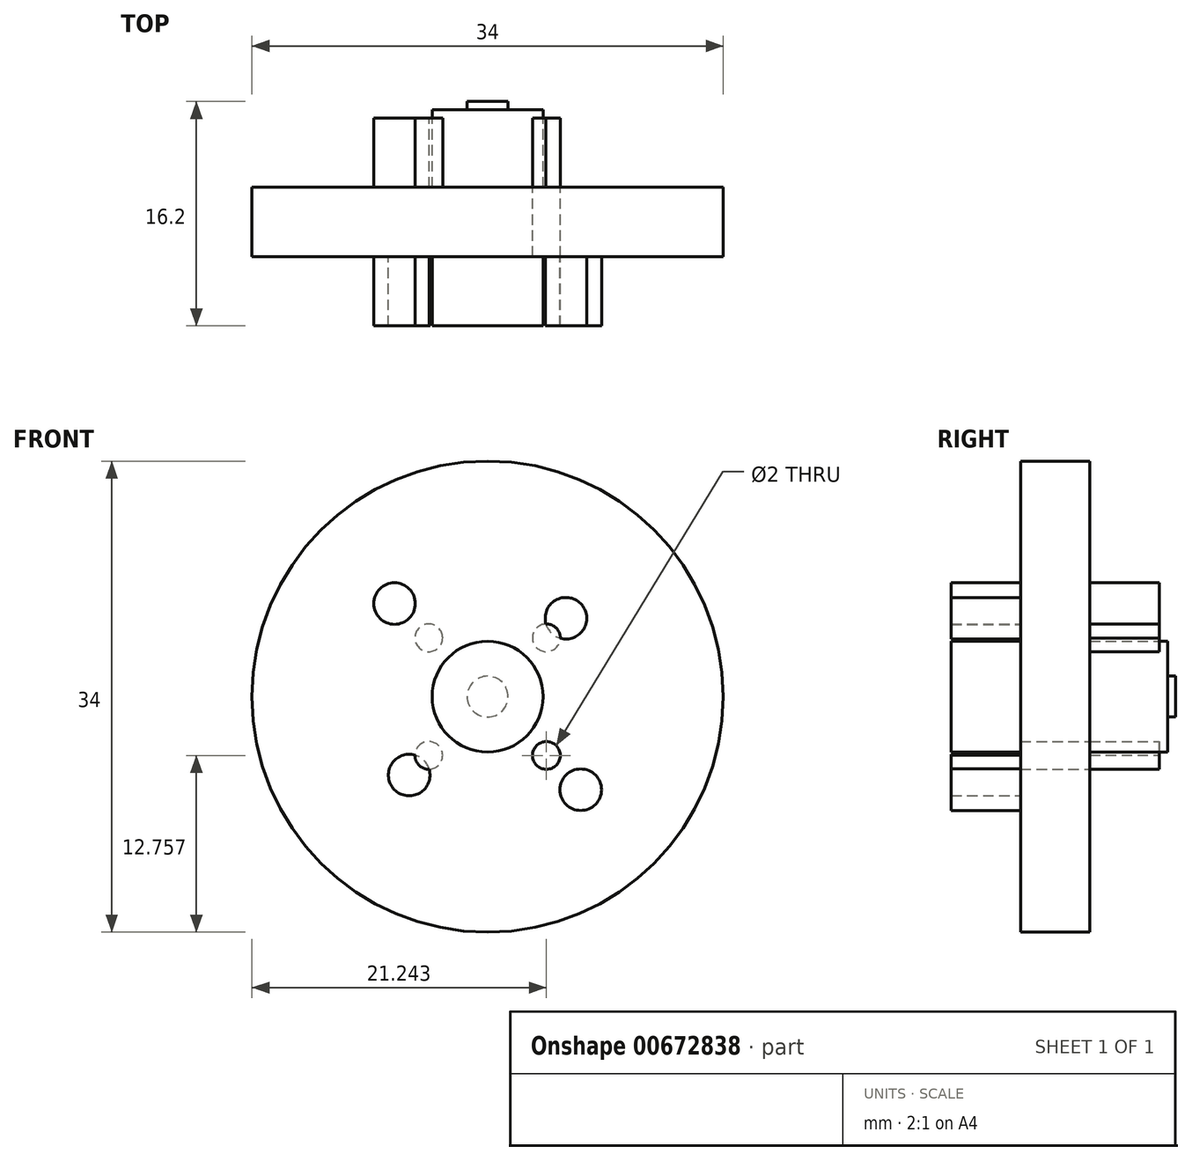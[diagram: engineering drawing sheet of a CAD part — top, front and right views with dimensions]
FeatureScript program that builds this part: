
annotation { "Feature Type Name" : "Feature", "Feature Type Description" : "" }
export const myFeature = defineFeature(function(context is Context, id is Id, definition is map)
    precondition{}
    {
        {
            var Q0;
            Q0=qCreatedBy(makeId("Front.planeOp"),FACE);
            var sketch = newSketch(context, id + "F0", { "sketchPlane" : qUnion([Q0])});
            skCircle(sketch, "E0", {"center": v(0, 0) * mm, "radius": 17 * mm});
            skCircle(sketch, "E1", {"center": v(5.66, 5.66) * mm, "radius": 1.5 * mm});
            skCircle(sketch, "E2.MirrorC", {"center": v(-6.72, 6.72) * mm, "radius": 1.5 * mm});
            skCircle(sketch, "E3.MirrorC", {"center": v(-5.66, -5.66) * mm, "radius": 1.5 * mm});
            skLineSegment(sketch, "E4", {"start": v(0, 29.65) * mm, "end": v(0, -28.8) * mm, "construction": true});
            skLineSegment(sketch, "E5", {"start": v(-6.72, 6.72) * mm, "end": v(4.6, -4.6) * mm, "construction": true});
            skLineSegment(sketch, "E6", {"start": v(5.66, 5.66) * mm, "end": v(-5.66, -5.66) * mm, "construction": true});
            skCircle(sketch, "E7", {"center": v(-4.24, 4.24) * mm, "radius": 1 * mm});
            skCircle(sketch, "E8.MirrorC", {"center": v(4.24, 4.24) * mm, "radius": 1 * mm});
            skCircle(sketch, "E9.MirrorC", {"center": v(4.24, -4.24) * mm, "radius": 1 * mm});
            skCircle(sketch, "E10.MirrorC", {"center": v(-4.24, -4.24) * mm, "radius": 1 * mm});
            skCircle(sketch, "E11.MirrorC", {"center": v(6.72, -6.72) * mm, "radius": 1.5 * mm});
            skCircle(sketch, "E12", {"center": v(0, 0) * mm, "radius": 1.48 * mm});
            skCircle(sketch, "E13", {"center": v(0, 0) * mm, "radius": 4 * mm});
            skSolve(sketch);
        }
        {
            var Q0;
            Q0=makeQuery(id+"F0.imprint","IMPRINT",FACE,{"disambiguationData":[TD([[makeQuery(id+"F0.imprint","IMPRINT",EDGE,{"derivedFrom":sQuery(id+"F0.wireOp",EDGE,"E0")}),1.0]])]});
            var Q1;
            {var subQ0=sQuery(id+"F0.wireOp",EDGE,"E7");var subQ1=sQuery(id+"F0.wireOp",EDGE,"E2.MirrorC");var subQ2=makeQuery(id+"F0.imprint","INTERSECT",VERTEX,{"disambiguationData":[OD(0.0)],"derivedFrom":[subQ1,subQ0]});Q1=makeQuery(id+"F0.imprint","IMPRINT",FACE,{"disambiguationData":[TD([[makeQuery(id+"F0.imprint","IMPRINT",EDGE,{"disambiguationData":[TD([[subQ2,-1.0]])],"derivedFrom":subQ1}),-1.0]])]});}
            var Q2;
            {var subQ0=sQuery(id+"F0.wireOp",EDGE,"E8.MirrorC");var subQ1=sQuery(id+"F0.wireOp",EDGE,"E1");var subQ2=makeQuery(id+"F0.imprint","INTERSECT",VERTEX,{"disambiguationData":[OD(0.0)],"derivedFrom":[subQ1,subQ0]});Q2=makeQuery(id+"F0.imprint","IMPRINT",FACE,{"disambiguationData":[TD([[makeQuery(id+"F0.imprint","IMPRINT",EDGE,{"disambiguationData":[TD([[subQ2,1.0]])],"derivedFrom":subQ1}),1.0]])]});}
            var Q3;
            {var subQ0=sQuery(id+"F0.wireOp",EDGE,"E8.MirrorC");var subQ1=sQuery(id+"F0.wireOp",EDGE,"E1");var subQ2=makeQuery(id+"F0.imprint","INTERSECT",VERTEX,{"disambiguationData":[OD(0.0)],"derivedFrom":[subQ1,subQ0]});Q3=makeQuery(id+"F0.imprint","IMPRINT",FACE,{"disambiguationData":[TD([[makeQuery(id+"F0.imprint","IMPRINT",EDGE,{"disambiguationData":[TD([[subQ2,-1.0]])],"derivedFrom":subQ1}),-1.0]])]});}
            var Q4;
            {var subQ0=sQuery(id+"F0.wireOp",EDGE,"E7");var subQ1=sQuery(id+"F0.wireOp",EDGE,"E2.MirrorC");var subQ2=makeQuery(id+"F0.imprint","INTERSECT",VERTEX,{"disambiguationData":[OD(0.0)],"derivedFrom":[subQ1,subQ0]});Q4=makeQuery(id+"F0.imprint","IMPRINT",FACE,{"disambiguationData":[TD([[makeQuery(id+"F0.imprint","IMPRINT",EDGE,{"disambiguationData":[TD([[subQ2,1.0]])],"derivedFrom":subQ1}),-1.0]])]});}
            var Q5;
            {var subQ0=sQuery(id+"F0.wireOp",EDGE,"E7");var subQ1=sQuery(id+"F0.wireOp",EDGE,"E2.MirrorC");var subQ2=makeQuery(id+"F0.imprint","INTERSECT",VERTEX,{"disambiguationData":[OD(0.0)],"derivedFrom":[subQ1,subQ0]});Q5=makeQuery(id+"F0.imprint","IMPRINT",FACE,{"disambiguationData":[TD([[makeQuery(id+"F0.imprint","IMPRINT",EDGE,{"disambiguationData":[TD([[subQ2,1.0]])],"derivedFrom":subQ1}),1.0]])]});}
            var Q6;
            {var subQ0=sQuery(id+"F0.wireOp",EDGE,"E10.MirrorC");var subQ1=sQuery(id+"F0.wireOp",EDGE,"E3.MirrorC");var subQ2=makeQuery(id+"F0.imprint","INTERSECT",VERTEX,{"disambiguationData":[OD(0.0)],"derivedFrom":[subQ1,subQ0]});Q6=makeQuery(id+"F0.imprint","IMPRINT",FACE,{"disambiguationData":[TD([[makeQuery(id+"F0.imprint","IMPRINT",EDGE,{"disambiguationData":[TD([[subQ2,-1.0]])],"derivedFrom":subQ1}),1.0]])]});}
            var Q7;
            {var subQ0=sQuery(id+"F0.wireOp",EDGE,"E10.MirrorC");var subQ1=sQuery(id+"F0.wireOp",EDGE,"E3.MirrorC");var subQ2=makeQuery(id+"F0.imprint","INTERSECT",VERTEX,{"disambiguationData":[OD(0.0)],"derivedFrom":[subQ1,subQ0]});Q7=makeQuery(id+"F0.imprint","IMPRINT",FACE,{"disambiguationData":[TD([[makeQuery(id+"F0.imprint","IMPRINT",EDGE,{"disambiguationData":[TD([[subQ2,1.0]])],"derivedFrom":subQ1}),1.0]])]});}
            var Q8;
            {var subQ0=sQuery(id+"F0.wireOp",EDGE,"E10.MirrorC");var subQ1=sQuery(id+"F0.wireOp",EDGE,"E3.MirrorC");var subQ2=makeQuery(id+"F0.imprint","INTERSECT",VERTEX,{"disambiguationData":[OD(0.0)],"derivedFrom":[subQ1,subQ0]});Q8=makeQuery(id+"F0.imprint","IMPRINT",FACE,{"disambiguationData":[TD([[makeQuery(id+"F0.imprint","IMPRINT",EDGE,{"disambiguationData":[TD([[subQ2,1.0]])],"derivedFrom":subQ1}),-1.0]])]});}
            var Q9;
            {var subQ0=sQuery(id+"F0.wireOp",EDGE,"E8.MirrorC");var subQ1=sQuery(id+"F0.wireOp",EDGE,"E1");var subQ2=makeQuery(id+"F0.imprint","INTERSECT",VERTEX,{"disambiguationData":[OD(0.0)],"derivedFrom":[subQ1,subQ0]});Q9=makeQuery(id+"F0.imprint","IMPRINT",FACE,{"disambiguationData":[TD([[makeQuery(id+"F0.imprint","IMPRINT",EDGE,{"disambiguationData":[TD([[subQ2,-1.0]])],"derivedFrom":subQ1}),1.0]])]});}
            var Q10;
            {var subQ0=sQuery(id+"F0.wireOp",EDGE,"E9.MirrorC");var subQ1=sQuery(id+"F0.wireOp",EDGE,"ca95e133-498b-419e-b427-ecf875a2ec590.MirrorC");var subQ2=makeQuery(id+"F0.imprint","INTERSECT",VERTEX,{"disambiguationData":[OD(0.0)],"derivedFrom":[subQ1,subQ0]});Q10=makeQuery(id+"F0.imprint","IMPRINT",FACE,{"disambiguationData":[TD([[makeQuery(id+"F0.imprint","IMPRINT",EDGE,{"disambiguationData":[TD([[subQ2,-1.0]])],"derivedFrom":subQ1}),1.0]])]});}
            var Q11;
            {var subQ0=sQuery(id+"F0.wireOp",EDGE,"E9.MirrorC");var subQ1=sQuery(id+"F0.wireOp",EDGE,"ca95e133-498b-419e-b427-ecf875a2ec590.MirrorC");var subQ2=makeQuery(id+"F0.imprint","INTERSECT",VERTEX,{"disambiguationData":[OD(0.0)],"derivedFrom":[subQ1,subQ0]});Q11=makeQuery(id+"F0.imprint","IMPRINT",FACE,{"disambiguationData":[TD([[makeQuery(id+"F0.imprint","IMPRINT",EDGE,{"disambiguationData":[TD([[subQ2,-1.0]])],"derivedFrom":subQ1}),-1.0]])]});}
            var Q12;
            {var subQ0=sQuery(id+"F0.wireOp",EDGE,"E9.MirrorC");var subQ1=sQuery(id+"F0.wireOp",EDGE,"ca95e133-498b-419e-b427-ecf875a2ec590.MirrorC");var subQ2=makeQuery(id+"F0.imprint","INTERSECT",VERTEX,{"disambiguationData":[OD(0.0)],"derivedFrom":[subQ1,subQ0]});Q12=makeQuery(id+"F0.imprint","IMPRINT",FACE,{"disambiguationData":[TD([[makeQuery(id+"F0.imprint","IMPRINT",EDGE,{"disambiguationData":[TD([[subQ2,1.0]])],"derivedFrom":subQ1}),-1.0]])]});}
            var Q13;
            Q13=makeQuery(id+"F0.imprint","IMPRINT",FACE,{"disambiguationData":[TD([[makeQuery(id+"F0.imprint","IMPRINT",EDGE,{"derivedFrom":sQuery(id+"F0.wireOp",EDGE,"E9.MirrorC")}),-1.0]])]});
            var Q14;
            Q14=makeQuery(id+"F0.imprint","IMPRINT",FACE,{"disambiguationData":[TD([[makeQuery(id+"F0.imprint","IMPRINT",EDGE,{"derivedFrom":sQuery(id+"F0.wireOp",EDGE,"E7")}),1.0]])]});
            var Q15;
            Q15=makeQuery(id+"F0.imprint","IMPRINT",FACE,{"disambiguationData":[TD([[makeQuery(id+"F0.imprint","IMPRINT",EDGE,{"derivedFrom":sQuery(id+"F0.wireOp",EDGE,"E2.MirrorC")}),-1.0]])]});
            var Q16;
            Q16=makeQuery(id+"F0.imprint","IMPRINT",FACE,{"disambiguationData":[TD([[makeQuery(id+"F0.imprint","IMPRINT",EDGE,{"derivedFrom":sQuery(id+"F0.wireOp",EDGE,"E11.MirrorC")}),1.0]])]});
            var Q17;
            Q17=makeQuery(id+"F0.imprint","IMPRINT",FACE,{"disambiguationData":[TD([[makeQuery(id+"F0.imprint","IMPRINT",EDGE,{"derivedFrom":sQuery(id+"F0.wireOp",EDGE,"E12")}),-1.0]])]});
            var Q18;
            Q18=makeQuery(id+"F0.imprint","IMPRINT",FACE,{"disambiguationData":[TD([[makeQuery(id+"F0.imprint","IMPRINT",EDGE,{"derivedFrom":sQuery(id+"F0.wireOp",EDGE,"E12")}),1.0]])]});
            extrude(context, id + "F1", {"entities" : qUnion([Q0, Q1, Q2, Q3, Q4, Q5, Q6, Q7, Q8, Q9, Q10, Q11, Q12, Q13, Q14, Q15, Q16, Q17, Q18]), "depth" : 15 * mm, "offsetDistance" : 25 * mm});
        }
        {
            var Q0;
            {var subQ0=sQuery(id+"F0.wireOp",EDGE,"E10.MirrorC");var subQ1=sQuery(id+"F0.wireOp",EDGE,"E3.MirrorC");var subQ2=makeQuery(id+"F0.imprint","INTERSECT",VERTEX,{"disambiguationData":[OD(0.0)],"derivedFrom":[subQ1,subQ0]});Q0=makeQuery(id+"F0.imprint","IMPRINT",FACE,{"disambiguationData":[TD([[makeQuery(id+"F0.imprint","IMPRINT",EDGE,{"disambiguationData":[TD([[subQ2,1.0]])],"derivedFrom":subQ1}),-1.0]])]});}
            var Q1;
            {var subQ0=sQuery(id+"F0.wireOp",EDGE,"E10.MirrorC");var subQ1=sQuery(id+"F0.wireOp",EDGE,"E3.MirrorC");var subQ2=makeQuery(id+"F0.imprint","INTERSECT",VERTEX,{"disambiguationData":[OD(0.0)],"derivedFrom":[subQ1,subQ0]});Q1=makeQuery(id+"F0.imprint","IMPRINT",FACE,{"disambiguationData":[TD([[makeQuery(id+"F0.imprint","IMPRINT",EDGE,{"disambiguationData":[TD([[subQ2,1.0]])],"derivedFrom":subQ1}),1.0]])]});}
            var Q2;
            Q2=makeQuery(id+"F0.imprint","IMPRINT",FACE,{"disambiguationData":[TD([[makeQuery(id+"F0.imprint","IMPRINT",EDGE,{"derivedFrom":sQuery(id+"F0.wireOp",EDGE,"E9.MirrorC")}),-1.0]])]});
            var Q3;
            {var subQ0=sQuery(id+"F0.wireOp",EDGE,"E8.MirrorC");var subQ1=sQuery(id+"F0.wireOp",EDGE,"E1");var subQ2=makeQuery(id+"F0.imprint","INTERSECT",VERTEX,{"disambiguationData":[OD(0.0)],"derivedFrom":[subQ1,subQ0]});Q3=makeQuery(id+"F0.imprint","IMPRINT",FACE,{"disambiguationData":[TD([[makeQuery(id+"F0.imprint","IMPRINT",EDGE,{"disambiguationData":[TD([[subQ2,-1.0]])],"derivedFrom":subQ1}),-1.0]])]});}
            var Q4;
            {var subQ0=sQuery(id+"F0.wireOp",EDGE,"E8.MirrorC");var subQ1=sQuery(id+"F0.wireOp",EDGE,"E1");var subQ2=makeQuery(id+"F0.imprint","INTERSECT",VERTEX,{"disambiguationData":[OD(0.0)],"derivedFrom":[subQ1,subQ0]});Q4=makeQuery(id+"F0.imprint","IMPRINT",FACE,{"disambiguationData":[TD([[makeQuery(id+"F0.imprint","IMPRINT",EDGE,{"disambiguationData":[TD([[subQ2,-1.0]])],"derivedFrom":subQ1}),1.0]])]});}
            var Q5;
            Q5=makeQuery(id+"F0.imprint","IMPRINT",FACE,{"disambiguationData":[TD([[makeQuery(id+"F0.imprint","IMPRINT",EDGE,{"derivedFrom":sQuery(id+"F0.wireOp",EDGE,"E7")}),1.0]])]});
            extrude(context, id + "F2", {"entities" : qUnion([Q0, Q1, Q2, Q3, Q4, Q5]), "operationType" : NewBodyOperationType.REMOVE, "depth" : 25 * mm, "hasSecondDirection" : true, "secondDirectionOppositeDirection" : false, "secondDirectionDepth" : 10 * mm});
        }
        {
            var Q0;
            {var subQ0=sQuery(id+"F0.wireOp",EDGE,"E7");var subQ1=sQuery(id+"F0.wireOp",EDGE,"E2.MirrorC");var subQ2=makeQuery(id+"F0.imprint","INTERSECT",VERTEX,{"disambiguationData":[OD(0.0)],"derivedFrom":[subQ1,subQ0]});Q0=makeQuery(id+"F0.imprint","IMPRINT",FACE,{"disambiguationData":[TD([[makeQuery(id+"F0.imprint","IMPRINT",EDGE,{"disambiguationData":[TD([[subQ2,-1.0]])],"derivedFrom":subQ1}),-1.0]])]});}
            var Q1;
            {var subQ0=sQuery(id+"F0.wireOp",EDGE,"E7");var subQ1=sQuery(id+"F0.wireOp",EDGE,"E2.MirrorC");var subQ2=makeQuery(id+"F0.imprint","INTERSECT",VERTEX,{"disambiguationData":[OD(0.0)],"derivedFrom":[subQ1,subQ0]});Q1=makeQuery(id+"F0.imprint","IMPRINT",FACE,{"disambiguationData":[TD([[makeQuery(id+"F0.imprint","IMPRINT",EDGE,{"disambiguationData":[TD([[subQ2,1.0]])],"derivedFrom":subQ1}),-1.0]])]});}
            var Q2;
            {var subQ0=sQuery(id+"F0.wireOp",EDGE,"E8.MirrorC");var subQ1=sQuery(id+"F0.wireOp",EDGE,"E1");var subQ2=makeQuery(id+"F0.imprint","INTERSECT",VERTEX,{"disambiguationData":[OD(0.0)],"derivedFrom":[subQ1,subQ0]});Q2=makeQuery(id+"F0.imprint","IMPRINT",FACE,{"disambiguationData":[TD([[makeQuery(id+"F0.imprint","IMPRINT",EDGE,{"disambiguationData":[TD([[subQ2,1.0]])],"derivedFrom":subQ1}),1.0]])]});}
            var Q3;
            {var subQ0=sQuery(id+"F0.wireOp",EDGE,"E8.MirrorC");var subQ1=sQuery(id+"F0.wireOp",EDGE,"E1");var subQ2=makeQuery(id+"F0.imprint","INTERSECT",VERTEX,{"disambiguationData":[OD(0.0)],"derivedFrom":[subQ1,subQ0]});Q3=makeQuery(id+"F0.imprint","IMPRINT",FACE,{"disambiguationData":[TD([[makeQuery(id+"F0.imprint","IMPRINT",EDGE,{"disambiguationData":[TD([[subQ2,-1.0]])],"derivedFrom":subQ1}),1.0]])]});}
            var Q4;
            {var subQ0=sQuery(id+"F0.wireOp",EDGE,"E9.MirrorC");var subQ1=sQuery(id+"F0.wireOp",EDGE,"ca95e133-498b-419e-b427-ecf875a2ec590.MirrorC");var subQ2=makeQuery(id+"F0.imprint","INTERSECT",VERTEX,{"disambiguationData":[OD(0.0)],"derivedFrom":[subQ1,subQ0]});Q4=makeQuery(id+"F0.imprint","IMPRINT",FACE,{"disambiguationData":[TD([[makeQuery(id+"F0.imprint","IMPRINT",EDGE,{"disambiguationData":[TD([[subQ2,1.0]])],"derivedFrom":subQ1}),-1.0]])]});}
            var Q5;
            {var subQ0=sQuery(id+"F0.wireOp",EDGE,"E9.MirrorC");var subQ1=sQuery(id+"F0.wireOp",EDGE,"ca95e133-498b-419e-b427-ecf875a2ec590.MirrorC");var subQ2=makeQuery(id+"F0.imprint","INTERSECT",VERTEX,{"disambiguationData":[OD(0.0)],"derivedFrom":[subQ1,subQ0]});Q5=makeQuery(id+"F0.imprint","IMPRINT",FACE,{"disambiguationData":[TD([[makeQuery(id+"F0.imprint","IMPRINT",EDGE,{"disambiguationData":[TD([[subQ2,-1.0]])],"derivedFrom":subQ1}),-1.0]])]});}
            var Q6;
            {var subQ0=sQuery(id+"F0.wireOp",EDGE,"E10.MirrorC");var subQ1=sQuery(id+"F0.wireOp",EDGE,"E3.MirrorC");var subQ2=makeQuery(id+"F0.imprint","INTERSECT",VERTEX,{"disambiguationData":[OD(0.0)],"derivedFrom":[subQ1,subQ0]});Q6=makeQuery(id+"F0.imprint","IMPRINT",FACE,{"disambiguationData":[TD([[makeQuery(id+"F0.imprint","IMPRINT",EDGE,{"disambiguationData":[TD([[subQ2,-1.0]])],"derivedFrom":subQ1}),1.0]])]});}
            var Q7;
            {var subQ0=sQuery(id+"F0.wireOp",EDGE,"E10.MirrorC");var subQ1=sQuery(id+"F0.wireOp",EDGE,"E3.MirrorC");var subQ2=makeQuery(id+"F0.imprint","INTERSECT",VERTEX,{"disambiguationData":[OD(0.0)],"derivedFrom":[subQ1,subQ0]});Q7=makeQuery(id+"F0.imprint","IMPRINT",FACE,{"disambiguationData":[TD([[makeQuery(id+"F0.imprint","IMPRINT",EDGE,{"disambiguationData":[TD([[subQ2,1.0]])],"derivedFrom":subQ1}),1.0]])]});}
            var Q8;
            Q8=makeQuery(id+"F0.imprint","IMPRINT",FACE,{"disambiguationData":[TD([[makeQuery(id+"F0.imprint","IMPRINT",EDGE,{"derivedFrom":sQuery(id+"F0.wireOp",EDGE,"E11.MirrorC")}),1.0]])]});
            var Q9;
            Q9=makeQuery(id+"F0.imprint","IMPRINT",FACE,{"disambiguationData":[TD([[makeQuery(id+"F0.imprint","IMPRINT",EDGE,{"derivedFrom":sQuery(id+"F0.wireOp",EDGE,"E2.MirrorC")}),-1.0]])]});
            extrude(context, id + "F3", {"entities" : qUnion([Q0, Q1, Q2, Q3, Q4, Q5, Q6, Q7, Q8, Q9]), "operationType" : NewBodyOperationType.REMOVE, "depth" : 5 * mm});
        }
        {
            var Q0;
            Q0=makeQuery(id+"F0.imprint","IMPRINT",FACE,{"disambiguationData":[TD([[makeQuery(id+"F0.imprint","IMPRINT",EDGE,{"derivedFrom":sQuery(id+"F0.wireOp",EDGE,"E12")}),-1.0]])]});
            extrude(context, id + "F4", {"entities" : qUnion([Q0]), "operationType" : NewBodyOperationType.ADD, "oppositeDirection" : true, "depth" : 0.6 * mm, "offsetDistance" : 25 * mm});
        }
        {
            var Q0;
            Q0=makeQuery(id+"F0.imprint","IMPRINT",FACE,{"disambiguationData":[TD([[makeQuery(id+"F0.imprint","IMPRINT",EDGE,{"derivedFrom":sQuery(id+"F0.wireOp",EDGE,"E12")}),1.0]])]});
            extrude(context, id + "F5", {"entities" : qUnion([Q0]), "operationType" : NewBodyOperationType.ADD, "oppositeDirection" : true, "depth" : 1.2 * mm, "offsetDistance" : 25 * mm});
        }
    });
